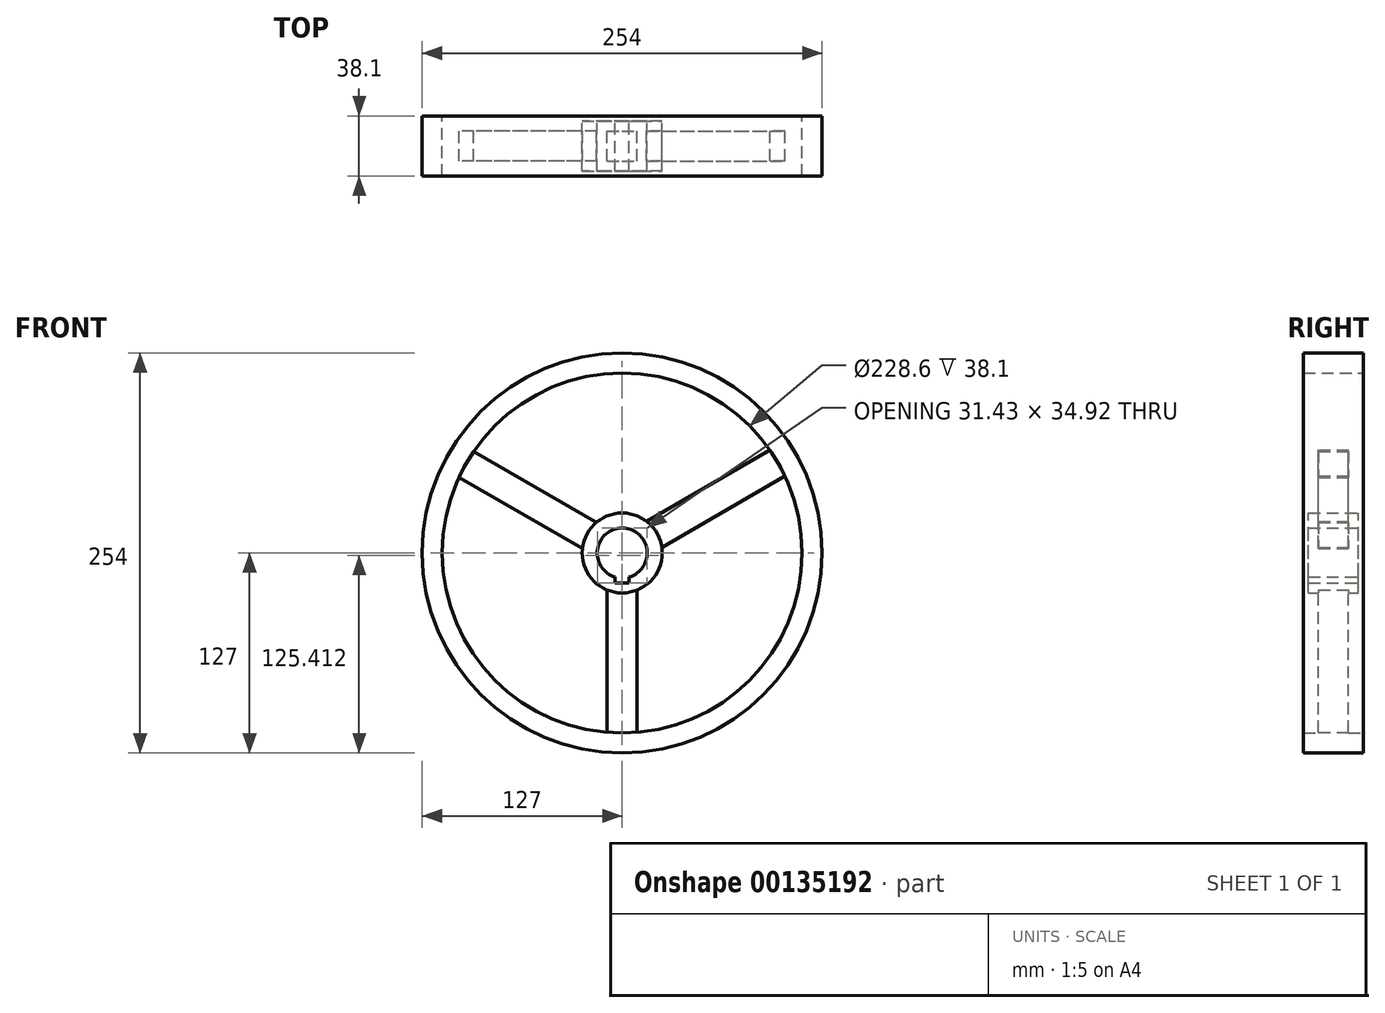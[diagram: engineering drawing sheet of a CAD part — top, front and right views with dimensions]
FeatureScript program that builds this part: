
annotation { "Feature Type Name" : "Feature", "Feature Type Description" : "" }
export const myFeature = defineFeature(function(context is Context, id is Id, definition is map)
    precondition{}
    {
        {
            var Q0;
            Q0=qCreatedBy(makeId("Front.planeOp"),FACE);
            var sketch = newSketch(context, id + "F0", { "sketchPlane" : qUnion([Q0])});
            skCircle(sketch, "E0", {"center": v(0, 0) * mm, "radius": 127 * mm});
            skCircle(sketch, "E1", {"center": v(0, 0) * mm, "radius": 114.3 * mm});
            skArc(sketch, "E2", {"start": v(4.45, -15.24) * mm, "mid": v(0, 15.88) * mm, "end": v(-4.45, -15.24) * mm});
            skCircle(sketch, "E3", {"center": v(0, 0) * mm, "radius": 25.4 * mm});
            skLineSegment(sketch, "E4", {"start": v(-9.52, -113.9) * mm, "end": v(-9.53, -23.55) * mm});
            skLineSegment(sketch, "E5", {"start": v(9.53, -113.9) * mm, "end": v(9.52, -23.55) * mm});
            skLineSegment(sketch, "E6", {"start": v(21.95, 12.79) * mm, "end": v(98.94, 57.24) * mm});
            skLineSegment(sketch, "E7", {"start": v(15.54, 20.09) * mm, "end": v(93.82, 65.28) * mm});
            skLineSegment(sketch, "E8", {"start": v(25.14, 3.63) * mm, "end": v(103.36, 48.8) * mm});
            skLineSegment(sketch, "E9", {"start": v(-22.35, 12.07) * mm, "end": v(-99.35, 56.52) * mm});
            skLineSegment(sketch, "E10", {"start": v(-16.24, 19.53) * mm, "end": v(-94.3, 64.6) * mm});
            skLineSegment(sketch, "E11", {"start": v(-25.25, 2.74) * mm, "end": v(-103.71, 48.04) * mm});
            skLineSegment(sketch, "E12", {"start": v(0, -25.4) * mm, "end": v(0, -114.3) * mm});
            skLineSegment(sketch, "E13", {"start": v(-4.45, -15.24) * mm, "end": v(-4.45, -19.05) * mm});
            skLineSegment(sketch, "E14", {"start": v(-4.45, -19.05) * mm, "end": v(4.45, -19.05) * mm});
            skLineSegment(sketch, "E15", {"start": v(4.45, -19.05) * mm, "end": v(4.45, -15.24) * mm});
            skSolve(sketch);
        }
        {
            var Q0;
            Q0=makeQuery(id+"F0.imprint","IMPRINT",FACE,{"disambiguationData":[TD([[makeQuery(id+"F0.imprint","IMPRINT",EDGE,{"derivedFrom":sQuery(id+"F0.wireOp",EDGE,"E0")}),1.0]])]});
            extrude(context, id + "F1", {"entities" : qUnion([Q0]), "endBound" : BoundingType.SYMMETRIC, "depth" : 38.1 * mm});
        }
        {
            var Q0;
            {var subQ0=sQuery(id+"F0.wireOp",EDGE,"E9");Q0=makeQuery(id+"F0.imprint","IMPRINT",FACE,{"disambiguationData":[TD([[makeQuery(id+"F0.imprint","IMPRINT",EDGE,{"derivedFrom":subQ0}),1.0]])]});}
            var Q1;
            {var subQ0=sQuery(id+"F0.wireOp",EDGE,"E9");Q1=makeQuery(id+"F0.imprint","IMPRINT",FACE,{"disambiguationData":[TD([[makeQuery(id+"F0.imprint","IMPRINT",EDGE,{"derivedFrom":subQ0}),-1.0]])]});}
            var Q2;
            {var subQ0=sQuery(id+"F0.wireOp",EDGE,"E6");Q2=makeQuery(id+"F0.imprint","IMPRINT",FACE,{"disambiguationData":[TD([[makeQuery(id+"F0.imprint","IMPRINT",EDGE,{"derivedFrom":subQ0}),1.0]])]});}
            var Q3;
            {var subQ0=sQuery(id+"F0.wireOp",EDGE,"E6");Q3=makeQuery(id+"F0.imprint","IMPRINT",FACE,{"disambiguationData":[TD([[makeQuery(id+"F0.imprint","IMPRINT",EDGE,{"derivedFrom":subQ0}),-1.0]])]});}
            var Q4;
            {var subQ0=sQuery(id+"F0.wireOp",EDGE,"E4");Q4=makeQuery(id+"F0.imprint","IMPRINT",FACE,{"disambiguationData":[TD([[makeQuery(id+"F0.imprint","IMPRINT",EDGE,{"derivedFrom":subQ0}),-1.0]])]});}
            var Q5;
            {var subQ0=sQuery(id+"F0.wireOp",EDGE,"E5");Q5=makeQuery(id+"F0.imprint","IMPRINT",FACE,{"disambiguationData":[TD([[makeQuery(id+"F0.imprint","IMPRINT",EDGE,{"derivedFrom":subQ0}),1.0]])]});}
            extrude(context, id + "F2", {"entities" : qUnion([Q0, Q1, Q2, Q3, Q4, Q5]), "operationType" : NewBodyOperationType.ADD, "endBound" : BoundingType.SYMMETRIC, "depth" : 19.05 * mm});
        }
        {
            var Q0;
            Q0=makeQuery(id+"F0.imprint","IMPRINT",FACE,{"disambiguationData":[TD([[makeQuery(id+"F0.imprint","IMPRINT",EDGE,{"derivedFrom":sQuery(id+"F0.wireOp",EDGE,"E2")}),-1.0]])]});
            extrude(context, id + "F3", {"entities" : qUnion([Q0]), "operationType" : NewBodyOperationType.ADD, "endBound" : BoundingType.SYMMETRIC, "depth" : 31.75 * mm});
        }
    });
